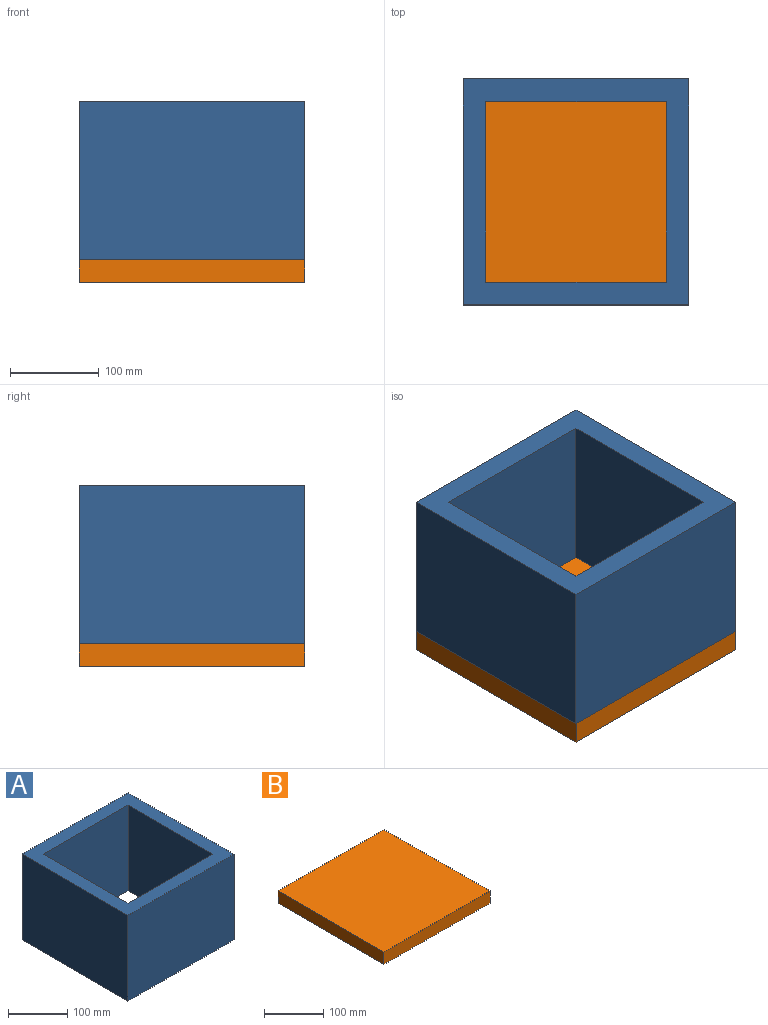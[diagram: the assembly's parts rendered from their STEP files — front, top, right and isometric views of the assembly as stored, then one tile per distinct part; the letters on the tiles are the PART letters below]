
ASSEMBLY  parts=2 mates=1
PART A: 10 faces, bbox 254x254x177.8 mm
  f0: plane 254x177.8mm, normal (0,1,0), area 45161.2mm2, adj f1,f7,f8,f9
  f1: plane 254x177.8mm, normal (-1,0,0), area 45161.2mm2, adj f0,f2,f8,f9
  f2: plane 254x177.8mm, normal (0,-1,0), area 45161.2mm2, adj f1,f7,f8,f9
  f3: plane 203.2x177.8mm, normal (1,0,0), area 36129mm2, adj f4,f6,f8,f9
  f4: plane 203.2x177.8mm, normal (0,-1,0), area 36129mm2, adj f3,f5,f8,f9
  f5: plane 203.2x177.8mm, normal (-1,0,0), area 36129mm2, adj f4,f6,f8,f9
  f6: plane 203.2x177.8mm, normal (0,1,0), area 36129mm2, adj f3,f5,f8,f9
  f7: plane 254x177.8mm, normal (1,0,0), area 45161.2mm2, adj f0,f2,f8,f9
  f8: plane 254x254mm, normal (0,0,1), area 23225.8mm2, adj f0,f1,f2,f3,f4,f5,f6,f7
  f9: plane 254x254mm, normal (0,0,-1), area 23225.8mm2, adj f0,f1,f2,f3,f4,f5,f6,f7
PART B: 6 faces, bbox 254x254x25.4 mm
  f0: plane 254x25.4mm, normal (0,1,0), area 6451.6mm2, adj f1,f3,f4,f5
  f1: plane 254x25.4mm, normal (-1,0,0), area 6451.6mm2, adj f0,f2,f4,f5
  f2: plane 254x25.4mm, normal (0,-1,0), area 6451.6mm2, adj f1,f3,f4,f5
  f3: plane 254x25.4mm, normal (1,0,0), area 6451.6mm2, adj f0,f2,f4,f5
  f4: plane 254x254mm, normal (0,0,1), area 64516mm2, adj f0,f1,f2,f3
  f5: plane 254x254mm, normal (0,0,-1), area 64516mm2, adj f0,f1,f2,f3
PLACE A t=(-180.58,-108.11,125.28)mm
PLACE B t=(55.82,-108.11,99.88)mm
MATE fastened A.f9 <-> B.f4  axis (0,0,-1) through (29.72,-108.11,125.28)mm
